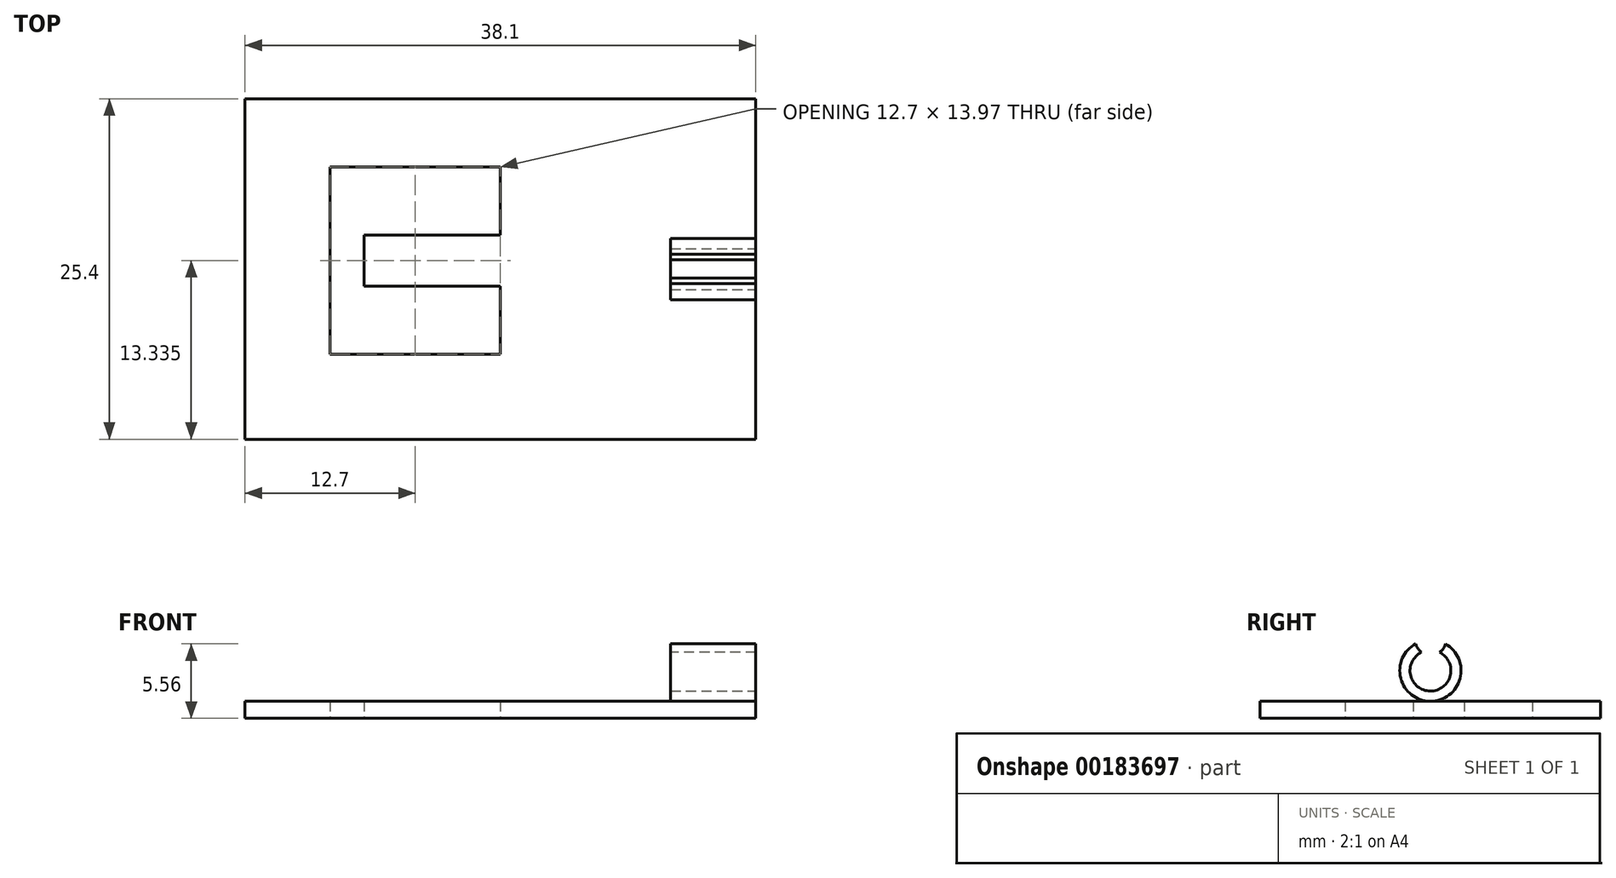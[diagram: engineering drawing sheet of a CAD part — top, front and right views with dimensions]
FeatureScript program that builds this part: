
annotation { "Feature Type Name" : "Feature", "Feature Type Description" : "" }
export const myFeature = defineFeature(function(context is Context, id is Id, definition is map)
    precondition{}
    {
        {
            var Q0;
            Q0=qCreatedBy(makeId("Top.planeOp"),FACE);
            var sketch = newSketch(context, id + "F0", { "sketchPlane" : qUnion([Q0])});
            skLineSegment(sketch, "E0", {"start": v(0, 0) * mm, "end": v(-38.1, 0) * mm});
            skLineSegment(sketch, "E1", {"start": v(-38.1, 0) * mm, "end": v(-38.1, 25.4) * mm});
            skLineSegment(sketch, "E2", {"start": v(-38.1, 25.4) * mm, "end": v(0, 25.4) * mm});
            skLineSegment(sketch, "E3", {"start": v(0, 25.4) * mm, "end": v(0, 0) * mm});
            skLineSegment(sketch, "E4", {"start": v(-38.1, 25.4) * mm, "end": v(-25.4, 25.4) * mm});
            skLineSegment(sketch, "E5", {"start": v(-38.1, 0) * mm, "end": v(-25.4, 0) * mm});
            skLineSegment(sketch, "E6", {"start": v(-25.4, 20.32) * mm, "end": v(-19.05, 20.32) * mm});
            skLineSegment(sketch, "E7", {"start": v(-25.4, 6.35) * mm, "end": v(-19.05, 6.35) * mm});
            skLineSegment(sketch, "E8", {"start": v(-25.4, 6.35) * mm, "end": v(-31.75, 6.35) * mm});
            skLineSegment(sketch, "E9", {"start": v(-25.4, 20.32) * mm, "end": v(-31.75, 20.32) * mm});
            skLineSegment(sketch, "E10", {"start": v(-31.75, 20.32) * mm, "end": v(-31.75, 6.35) * mm});
            skLineSegment(sketch, "E11", {"start": v(-19.05, 20.32) * mm, "end": v(-19.05, 15.24) * mm});
            skLineSegment(sketch, "E12", {"start": v(-19.05, 6.35) * mm, "end": v(-19.05, 11.43) * mm});
            skLineSegment(sketch, "E13", {"start": v(-19.05, 11.43) * mm, "end": v(-29.21, 11.43) * mm});
            skLineSegment(sketch, "E14", {"start": v(-19.05, 15.24) * mm, "end": v(-29.21, 15.24) * mm});
            skLineSegment(sketch, "E15", {"start": v(-29.21, 15.24) * mm, "end": v(-29.21, 11.43) * mm});
            skSolve(sketch);
        }
        {
            var Q0;
            Q0=makeQuery(id+"F0.imprint","IMPRINT",FACE,{"disambiguationData":[TD([[makeQuery(id+"F0.imprint","IMPRINT",EDGE,{"derivedFrom":sQuery(id+"F0.wireOp",EDGE,"E0")}),-1.0]])]});
            extrude(context, id + "F1", {"entities" : qUnion([Q0]), "depth" : 1.27 * mm});
        }
        {
            var Q0;
            Q0=qCreatedBy(makeId("Right.planeOp"),FACE);
            var sketch = newSketch(context, id + "F2", { "sketchPlane" : qUnion([Q0])});
            skLineSegment(sketch, "E16", {"start": v(0, 0) * mm, "end": v(12.7, 0) * mm});
            skLineSegment(sketch, "E17", {"start": v(12.7, 0) * mm, "end": v(12.7, 3.56) * mm});
            skCircle(sketch, "E18", {"center": v(12.7, 3.56) * mm, "radius": 1.52 * mm});
            skCircle(sketch, "E19", {"center": v(12.7, 3.56) * mm, "radius": 2.29 * mm});
            skSolve(sketch);
        }
        {
            var Q0;
            Q0 = qSketchRegion(id + "F2", true);
            extrude(context, id + "F3", {"entities" : qUnion([Q0]), "oppositeDirection" : true, "depth" : 6.35 * mm});
        }
        {
            var Q0;
            Q0=makeQuery(id+"F3.opExtrude","CAP_FACE",FACE,{"disambiguationData":[OSD([sQuery(id+"F2.wireOp",EDGE,"E18"),sQuery(id+"F2.wireOp",EDGE,"E19")])],"isStart":false});
            var sketch = newSketch(context, id + "F4", { "sketchPlane" : qUnion([Q0])});
            skLineSegment(sketch, "E20", {"start": v(-12.71, 1.27) * mm, "end": v(-12.71, 5.84) * mm});
            skLineSegment(sketch, "E21", {"start": v(-12.71, 5.84) * mm, "end": v(-13.98, 5.83) * mm});
            skLineSegment(sketch, "E22", {"start": v(-12.71, 5.84) * mm, "end": v(-11.44, 5.85) * mm});
            skLineSegment(sketch, "E23", {"start": v(-11.44, 5.85) * mm, "end": v(-12.71, 3.56) * mm});
            skLineSegment(sketch, "E24", {"start": v(-12.71, 3.56) * mm, "end": v(-13.98, 5.83) * mm});
            skSolve(sketch);
        }
        {
            var Q0;
            Q0=sQuery(id+"F4.wireOp",VERTEX,"E22.start");
            var Q1;
            Q1=makeQuery(id+"F3.opExtrude","SWEPT_BODY",BODY,{"disambiguationData":[OSD([sQuery(id+"F2.wireOp",EDGE,"E18"),sQuery(id+"F2.wireOp",EDGE,"E19")])]});
            hole(context, id + "F5", {"style" : HoleStyle.SIMPLE, "endStyle" : HoleEndStyle.BLIND, "holeDiameter" : 2.3 * mm, "holeDepth" : 25.4 * mm, "locations" : qUnion([Q0]), "scope" : qUnion([Q1])});
        }
    });
